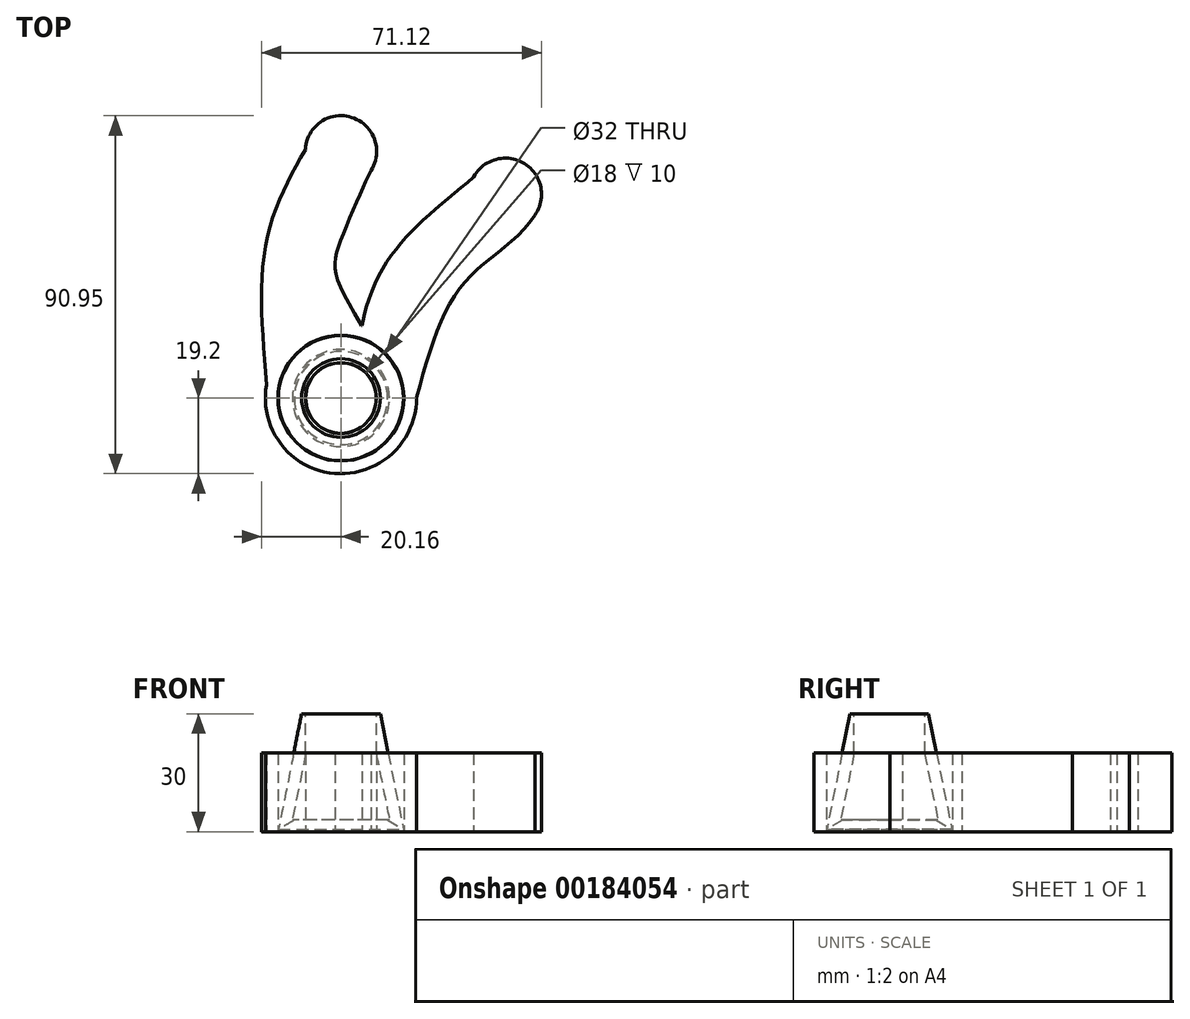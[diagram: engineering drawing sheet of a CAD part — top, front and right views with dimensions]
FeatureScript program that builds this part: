
annotation { "Feature Type Name" : "Feature", "Feature Type Description" : "" }
export const myFeature = defineFeature(function(context is Context, id is Id, definition is map)
    precondition{}
    {
        {
            var Q0;
            Q0=qCreatedBy(makeId("Top.planeOp"),FACE);
            var sketch = newSketch(context, id + "F0", { "sketchPlane" : qUnion([Q0])});
            skCircle(sketch, "E0", {"center": v(0, 0) * mm, "radius": 16 * mm});
            skCircle(sketch, "E1", {"center": v(0, 0) * mm, "radius": 19.2 * mm});
            skCircle(sketch, "E2", {"center": v(0, 62.7) * mm, "radius": 9.05 * mm});
            skCircle(sketch, "E3", {"center": v(41.77, 51.77) * mm, "radius": 9.19 * mm});
            skFitSpline(sketch, "E4", {"points": [v(-18.9, 3.36) * mm, v(-18.9, 40.12) * mm, v(-9.03, 63.17) * mm], "startDerivative": vector(-6.08, 73.95) * mm, "endDerivative": vector(26.97, 47.55) * mm});
            skFitSpline(sketch, "E5", {"points": [v(5.3, 18.45) * mm, v(0, 40.18) * mm, v(7.7, 57.95) * mm], "startDerivative": vector(-45.5, 74.2) * mm, "endDerivative": vector(3.63, 5.69) * mm});
            skFitSpline(sketch, "E6", {"points": [v(5.3, 18.45) * mm, v(15.89, 40.14) * mm, v(33.72, 56.2) * mm], "startDerivative": vector(11.26, 55.27) * mm, "endDerivative": vector(36.25, 31.8) * mm});
            skFitSpline(sketch, "E7", {"points": [v(16.55, -9.72) * mm, v(31.26, 29.21) * mm, v(49.81, 47.33) * mm], "startDerivative": vector(25.22, 92.33) * mm, "endDerivative": vector(30.89, 52.35) * mm});
            skSolve(sketch);
        }
        {
            var Q0;
            Q0=qCreatedBy(makeId("Top.planeOp"),FACE);
            cPlane(context, id + "F1", {"entities" : qUnion([Q0]), "cplaneType" : CPlaneType.OFFSET, "offset" : 30 * mm, "width" : 150 * mm, "height" : 150 * mm});
        }
        {
            var Q0;
            Q0=qCreatedBy(id+"F1.planeOp",FACE);
            var sketch = newSketch(context, id + "F2", { "sketchPlane" : qUnion([Q0])});
            skCircle(sketch, "E8", {"center": v(0, 0) * mm, "radius": 10 * mm});
            skSolve(sketch);
        }
        {
            var Q0;
            Q0=makeQuery(id+"F0.imprint","IMPRINT",FACE,{"disambiguationData":[TD([[makeQuery(id+"F0.imprint","IMPRINT",EDGE,{"derivedFrom":sQuery(id+"F0.wireOp",EDGE,"E0")}),1.0]])]});
            var Q1;
            Q1=makeQuery(id+"F2.imprint","IMPRINT",FACE,{"disambiguationData":[TD([[makeQuery(id+"F2.imprint","IMPRINT",EDGE,{"derivedFrom":sQuery(id+"F2.wireOp",EDGE,"E8")}),1.0]])]});
            loft(context, id + "F3", {"sheetProfilesArray" : [{ "sheetProfileEntities" : qUnion([Q0]) }, { "sheetProfileEntities" : qUnion([Q1]) }]});
        }
        {
            var Q0;
            Q0=makeQuery(id+"F3.opLoft","SWEPT_FACE",FACE,{"disambiguationData":[OSD([sQuery(id+"F0.wireOp",EDGE,"E0"),sQuery(id+"F2.wireOp",EDGE,"E8")])]});
            var Q1;
            Q1=makeQuery(id+"F3.opLoft","SWEPT_BODY",BODY,{"disambiguationData":[OSD([makeQuery(id+"F0.imprint","IMPRINT",FACE,{"disambiguationData":[TD([[makeQuery(id+"F0.imprint","IMPRINT",EDGE,{"derivedFrom":sQuery(id+"F0.wireOp",EDGE,"E0")}),1.0]])]}),makeQuery(id+"F2.imprint","IMPRINT",FACE,{"disambiguationData":[TD([[makeQuery(id+"F2.imprint","IMPRINT",EDGE,{"derivedFrom":sQuery(id+"F2.wireOp",EDGE,"E8")}),1.0]])]})])]});
            shell(context, id + "F4", {"isHollow" : true, "entities" : qUnion([Q0]), "parts" : qUnion([Q1]), "thickness" : 3 * mm});
        }
        {
            var Q0;
            {var subQ0=sQuery(id+"F0.wireOp",EDGE,"6SLrMwwr-dSHt-PD3u-omMm-QyfazCrkuMBX");var subQ1=sQuery(id+"F0.wireOp",EDGE,"E2");var subQ2=makeQuery(id+"F0.imprint","INTERSECT",VERTEX,{"derivedFrom":[subQ1,subQ0]});Q0=makeQuery(id+"F0.imprint","IMPRINT",FACE,{"disambiguationData":[TD([[makeQuery(id+"F0.imprint","IMPRINT",EDGE,{"disambiguationData":[TD([[subQ2,-1.0]])],"derivedFrom":subQ1}),-1.0]])]});}
            var Q1;
            {var subQ0=sQuery(id+"F0.wireOp",EDGE,"E2");var subQ1=makeQuery(id+"F0.imprint","INTERSECT",VERTEX,{"derivedFrom":[subQ0,sQuery(id+"F0.wireOp",EDGE,"6SLrMwwr-dSHt-PD3u-omMm-QyfazCrkuMBX")]});Q1=makeQuery(id+"F0.imprint","IMPRINT",FACE,{"disambiguationData":[TD([[makeQuery(id+"F0.imprint","IMPRINT",EDGE,{"disambiguationData":[TD([[subQ1,1.0]])],"derivedFrom":subQ0}),1.0]])]});}
            var Q2;
            Q2=makeQuery(id+"F0.imprint","IMPRINT",FACE,{"disambiguationData":[TD([[makeQuery(id+"F0.imprint","IMPRINT",EDGE,{"derivedFrom":sQuery(id+"F0.wireOp",EDGE,"E0")}),-1.0]])]});
            var Q3;
            {var subQ0=sQuery(id+"F0.wireOp",EDGE,"E3");var subQ1=makeQuery(id+"F0.imprint","INTERSECT",VERTEX,{"derivedFrom":[sQuery(id+"F0.wireOp",EDGE,"8UWX5MlC-xHg9-qTy2-MJ1w-iYILyikVTW8m"),subQ0]});Q3=makeQuery(id+"F0.imprint","IMPRINT",FACE,{"disambiguationData":[TD([[makeQuery(id+"F0.imprint","IMPRINT",EDGE,{"disambiguationData":[TD([[subQ1,-1.0]])],"derivedFrom":subQ0}),1.0]])]});}
            var Q4;
            {var subQ0=sQuery(id+"F0.wireOp",EDGE,"8UWX5MlC-xHg9-qTy2-MJ1w-iYILyikVTW8m");Q4=makeQuery(id+"F0.imprint","IMPRINT",FACE,{"disambiguationData":[TD([[makeQuery(id+"F0.imprint","IMPRINT",EDGE,{"derivedFrom":subQ0}),-1.0]])]});}
            var Q5;
            {var subQ0=sQuery(id+"F0.wireOp",EDGE,"E6");Q5=makeQuery(id+"F0.imprint","IMPRINT",FACE,{"disambiguationData":[TD([[makeQuery(id+"F0.imprint","IMPRINT",EDGE,{"derivedFrom":subQ0}),-1.0]])]});}
            extrude(context, id + "F5", {"entities" : qUnion([Q0, Q1, Q2, Q3, Q4, Q5]), "depth" : 20 * mm});
        }
        {
            var Q0;
            Q0=sQuery(id+"F2.wireOp",VERTEX,"E8.center");
            var Q1;
            Q1=makeQuery(id+"F3.opLoft","SWEPT_BODY",BODY,{"disambiguationData":[OSD([makeQuery(id+"F0.imprint","IMPRINT",FACE,{"disambiguationData":[TD([[makeQuery(id+"F0.imprint","IMPRINT",EDGE,{"derivedFrom":sQuery(id+"F0.wireOp",EDGE,"E0")}),1.0]])]}),makeQuery(id+"F2.imprint","IMPRINT",FACE,{"disambiguationData":[TD([[makeQuery(id+"F2.imprint","IMPRINT",EDGE,{"derivedFrom":sQuery(id+"F2.wireOp",EDGE,"E8")}),1.0]])]})])]});
            hole(context, id + "F6", {"style" : HoleStyle.SIMPLE, "endStyle" : HoleEndStyle.BLIND, "holeDiameter" : 18 * mm, "holeDepth" : 10 * mm, "locations" : qUnion([Q0]), "scope" : qUnion([Q1])});
        }
        {
            var Q0;
            Q0=sQuery(id+"F0.wireOp",VERTEX,"E1.center");
            var Q1;
            Q1=makeQuery(id+"F3.opLoft","SWEPT_BODY",BODY,{"disambiguationData":[OSD([makeQuery(id+"F0.imprint","IMPRINT",FACE,{"disambiguationData":[TD([[makeQuery(id+"F0.imprint","IMPRINT",EDGE,{"derivedFrom":sQuery(id+"F0.wireOp",EDGE,"E0")}),1.0]])]}),makeQuery(id+"F2.imprint","IMPRINT",FACE,{"disambiguationData":[TD([[makeQuery(id+"F2.imprint","IMPRINT",EDGE,{"derivedFrom":sQuery(id+"F2.wireOp",EDGE,"E8")}),1.0]])]})])]});
            hole(context, id + "F7", {"style" : HoleStyle.SIMPLE, "endStyle" : HoleEndStyle.BLIND, "oppositeDirection" : true, "holeDiameter" : 32 * mm, "holeDepth" : .5 * mm, "locations" : qUnion([Q0]), "scope" : qUnion([Q1])});
        }
    });
